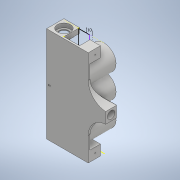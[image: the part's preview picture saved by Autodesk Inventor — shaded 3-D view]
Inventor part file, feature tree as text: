
AUTODESK INVENTOR PART (.ipt)
format: ipt  version: 2020 (Build 240168000, 168)  size: 863,744 bytes
history: native  units: mm
features: sketch x32, extrude x29, fillet x6
ambient origin geometry x8: Origin, YZ Plane, XZ Plane, XY Plane, X Axis, Y Axis, Z Axis, Center Point
bodies: Solid1 (feature_tree)
feature tree (67):
  extrude  "Extrusion1"  Depth=165.0mm
  extrude  "Extrusion2"  Depth=8.5mm
  extrude  "Extrusion3"  Depth=25.0mm TaperAngle=0.0deg
  extrude  "Extrusion4"  Depth=25.0mm
  extrude  "Extrusion5"  Depth=7.1mm
  extrude  "Extrusion6"  Depth=7.1mm TaperAngle=0.0deg
  fillet  "Fillet1"  Radius=5.0mm
  extrude  "Extrusion7"  Depth=10.0mm TaperAngle=0.0deg
  fillet  "Fillet2"  Radius=2.0mm
  extrude  "Extrusion8"  Depth=8.0mm
  extrude  "Extrusion9"  Depth=16.0mm
  fillet  "Fillet3"  Radius=8.0mm
  extrude  "Extrusion10"  Depth=6.0mm
  extrude  "Extrusion11"  Depth=3.5mm
  sketch  "Sketch12"  dims[d32=12.25mm d33=3.5mm]
  sketch  "Sketch13"  dims[d34=12.25mm d35=12.25mm]
  extrude  "Extrusion12"  Depth=3.5mm
  extrude  "Extrusion13"  Depth=12.25mm
  sketch  "Sketch16"  dims[d41=8.0mm d42=1.0mm]
  extrude  "Extrusion14"  Depth=40.0mm TaperAngle=0.0deg
  extrude  "Extrusion15"  Depth=2.0mm
  extrude  "Extrusion16"  Depth=1.0mm
  extrude  "Extrusion17"  Depth=2.0mm TaperAngle=0.0deg
  extrude  "Extrusion18"  Depth=7.1mm TaperAngle=0.0deg
  fillet  "Fillet4"  Radius=3.0mm
  extrude  "Extrusion19"  Depth=42.0mm
  extrude  "Extrusion20"  Depth=42.0mm
  extrude  "Extrusion21"  Depth=42.0mm
  extrude  "Extrusion22"  Depth=2.0mm
  extrude  "Extrusion23"  Depth=2.0mm
  extrude  "Extrusion24"  Depth=45.0mm TaperAngle=0.0deg
  fillet  "Fillet5"  Radius=10.0mm
  extrude  "Extrusion25"  Depth=2.0mm TaperAngle=0.0deg
  fillet  "Fillet6"  Radius=2.0mm
  extrude  "Extrusion26"  Depth=2.0mm
  extrude  "Extrusion27"  Depth=2.0mm
  extrude  "Extrusion28"  Depth=7.0mm TaperAngle=0.0deg
  extrude  "Extrusion29"  Depth=1.0mm
  sketch  "Sketch1"  dims[d0=25.0mm d1=165.0mm]
  sketch  "Sketch2"  dims[d2=3.0mm d3=0.0mm d4=8.5mm]
  sketch  "Sketch3"  dims[d5=8.5mm d6=25.0mm d7=0.0mm]
  sketch  "Sketch4"  dims[d8=25.0mm d9=22.75mm]
  sketch  "Sketch5"  dims[d10=7.1mm d11=0.0mm d12=15.5mm]
  sketch  "Sketch6"  dims[d13=165.0mm d14=0.0mm d15=7.1mm d16=0.0mm d17=5.0mm]
  sketch  "Sketch7"  dims[d18=5.0mm d19=10.0mm d20=0.0mm d21=2.0mm]
  sketch  "Sketch8"  dims[d22=16.0mm d23=8.0mm]
  sketch  "Sketch9"  dims[d24=16.0mm d25=16.0mm d26=8.0mm]
  sketch  "Sketch10"  dims[d27=45.0mm d28=0.0mm d29=6.0mm]
  sketch  "Sketch11"  dims[d30=12.25mm d31=3.5mm]
  sketch  "Sketch14"  dims[d36=3.5mm d37=40.0mm d38=0.0mm]
  sketch  "Sketch15"  dims[d39=1.0mm d40=2.0mm]
  sketch  "Sketch17"  dims[d43=2.0mm d44=12.0mm d45=0.0mm]
  sketch  "Sketch18"  dims[d46=6.0mm d47=7.1mm d48=0.0mm d49=3.0mm d50=0.0mm]
  sketch  "Sketch19"  dims[d51=42.0mm d52=38.75mm]
  sketch  "Sketch20"  dims[d53=42.0mm d54=38.75mm]
  sketch  "Sketch21"  dims[d55=42.0mm d56=38.75mm]
  sketch  "Sketch22"  dims[d57=45.0mm d58=0.0mm d59=2.0mm]
  sketch  "Sketch23"  dims[d60=4.0mm d61=2.0mm]
  sketch  "Sketch24"  dims[d62=4.0mm d63=45.0mm d64=0.0mm d65=10.0mm]
  sketch  "Sketch25"  dims[d66=12.0mm d67=0.0mm d68=2.0mm d69=0.0mm d70=2.0mm d71=0.0mm]
  sketch  "Sketch26"  dims[d72=2.0mm d73=2.0mm]
  sketch  "Sketch27"  dims[d74=5.0mm d75=0.0mm d76=2.0mm]
  sketch  "Sketch28"  dims[d77=2.0mm d78=7.0mm d79=0.0mm]
  sketch  "Sketch29"  dims[d80=1.0mm d81=0.25mm]
  sketch  "Sketch30"  dims[d82=0.25mm]
  sketch  "Sketch31"  dims[d83=44.75mm d84=0.0mm]
  sketch  "Sketch32"  dims[d85=44.0mm d86=0.0mm d87=22.6mm d88=8.5mm d89=0.0mm d90=22.6mm d91=8.5mm d92=0.0mm d93=27.0mm d94=0.0mm d95=60.0mm d96=19.05mm d97=3.0mm d98=0.0mm d99=31.75mm d100=19.05mm d101=19.05mm d102=31.5mm d103=0.0mm d104=38.0mm d105=12.954mm d106=27.5mm d107=0.0mm d108=18.0mm d109=18.0mm d110=18.0mm d111=18.0mm d112=18.0mm d113=0.0mm d114=2.0mm d115=2.0mm d116=2.0mm d117=5.0mm d118=0.0mm d119=10.0mm d120=148.0mm d121=0.0mm]
